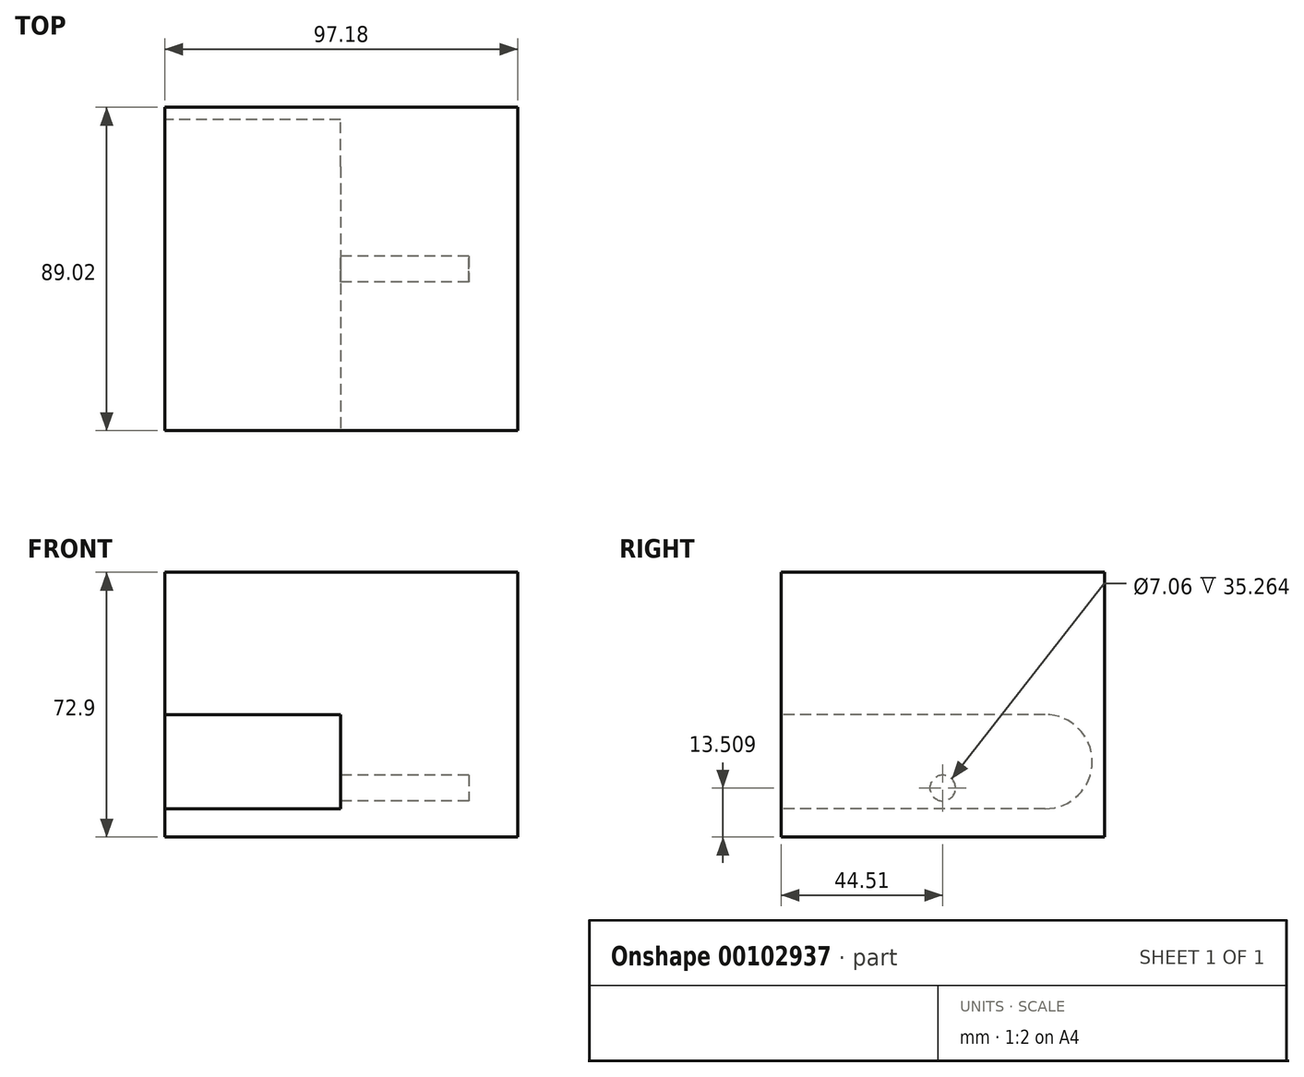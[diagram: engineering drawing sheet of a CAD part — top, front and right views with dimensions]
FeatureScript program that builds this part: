
annotation { "Feature Type Name" : "Feature", "Feature Type Description" : "" }
export const myFeature = defineFeature(function(context is Context, id is Id, definition is map)
    precondition{}
    {
        {
            var Q0;
            Q0=qCreatedBy(makeId("Front.planeOp"),FACE);
            var sketch = newSketch(context, id + "F0", { "sketchPlane" : qUnion([Q0])});
            skLineSegment(sketch, "E0.bottom", {"start": v(-48.6, 36.45) * mm, "end": v(48.6, 36.45) * mm});
            skLineSegment(sketch, "E0.top", {"start": v(-48.6, -36.45) * mm, "end": v(48.6, -36.45) * mm});
            skLineSegment(sketch, "E0.left", {"start": v(-48.6, 36.45) * mm, "end": v(-48.6, -36.45) * mm});
            skLineSegment(sketch, "E0.right", {"start": v(48.6, 36.45) * mm, "end": v(48.6, -36.45) * mm});
            skPoint(sketch, "E0.middle", {"position": v(0, 0) * mm});
            skSolve(sketch);
        }
        {
            var Q0;
            Q0 = qSketchRegion(id + "F0", true);
            extrude(context, id + "F1", {"entities" : qUnion([Q0]), "endBound" : BoundingType.SYMMETRIC, "oppositeDirection" : true, "depth" : 89.02 * mm});
        }
        {
            var Q0;
            Q0=makeQuery(id+"F1.opExtrude","SWEPT_FACE",FACE,{"disambiguationData":[OSD([sQuery(id+"F0.wireOp",EDGE,"E0.left")])]});
            var sketch = newSketch(context, id + "F2", { "sketchPlane" : qUnion([Q0])});
            skArc(sketch, "E1", {"start": v(-28.18, -2.7) * mm, "mid": v(-41.15, -15.68) * mm, "end": v(-28.18, -28.65) * mm});
            skLineSegment(sketch, "E2", {"start": v(-28.18, -28.65) * mm, "end": v(44.51, -28.65) * mm});
            skLineSegment(sketch, "E3", {"start": v(-28.18, -2.7) * mm, "end": v(44.51, -2.7) * mm});
            skLineSegment(sketch, "E4", {"start": v(44.51, -28.65) * mm, "end": v(44.51, -2.7) * mm});
            skSolve(sketch);
        }
        {
            var Q0;
            Q0 = qSketchRegion(id + "F2", true);
            extrude(context, id + "F3", {"entities" : qUnion([Q0]), "operationType" : NewBodyOperationType.REMOVE, "oppositeDirection" : true, "depth" : 48.42 * mm});
        }
        {
            var Q0;
            Q0=makeQuery(id+"F3.boolean.opBoolean","COPY",FACE,{"derivedFrom":makeQuery(id+"F3.opExtrude","CAP_FACE",FACE,{"disambiguationData":[OSD([sQuery(id+"F2.wireOp",EDGE,"E1"),sQuery(id+"F2.wireOp",EDGE,"E2"),sQuery(id+"F2.wireOp",EDGE,"E3"),sQuery(id+"F2.wireOp",EDGE,"E4")])],"isStart":false})});
            var sketch = newSketch(context, id + "F4", { "sketchPlane" : qUnion([Q0])});
            skCircle(sketch, "E5", {"center": v(0, -22.94) * mm, "radius": 3.53 * mm});
            skSolve(sketch);
        }
        {
            var Q0;
            Q0 = qSketchRegion(id + "F4", true);
            extrude(context, id + "F5", {"entities" : qUnion([Q0]), "operationType" : NewBodyOperationType.REMOVE, "oppositeDirection" : true, "depth" : 35.26 * mm});
        }
    });
